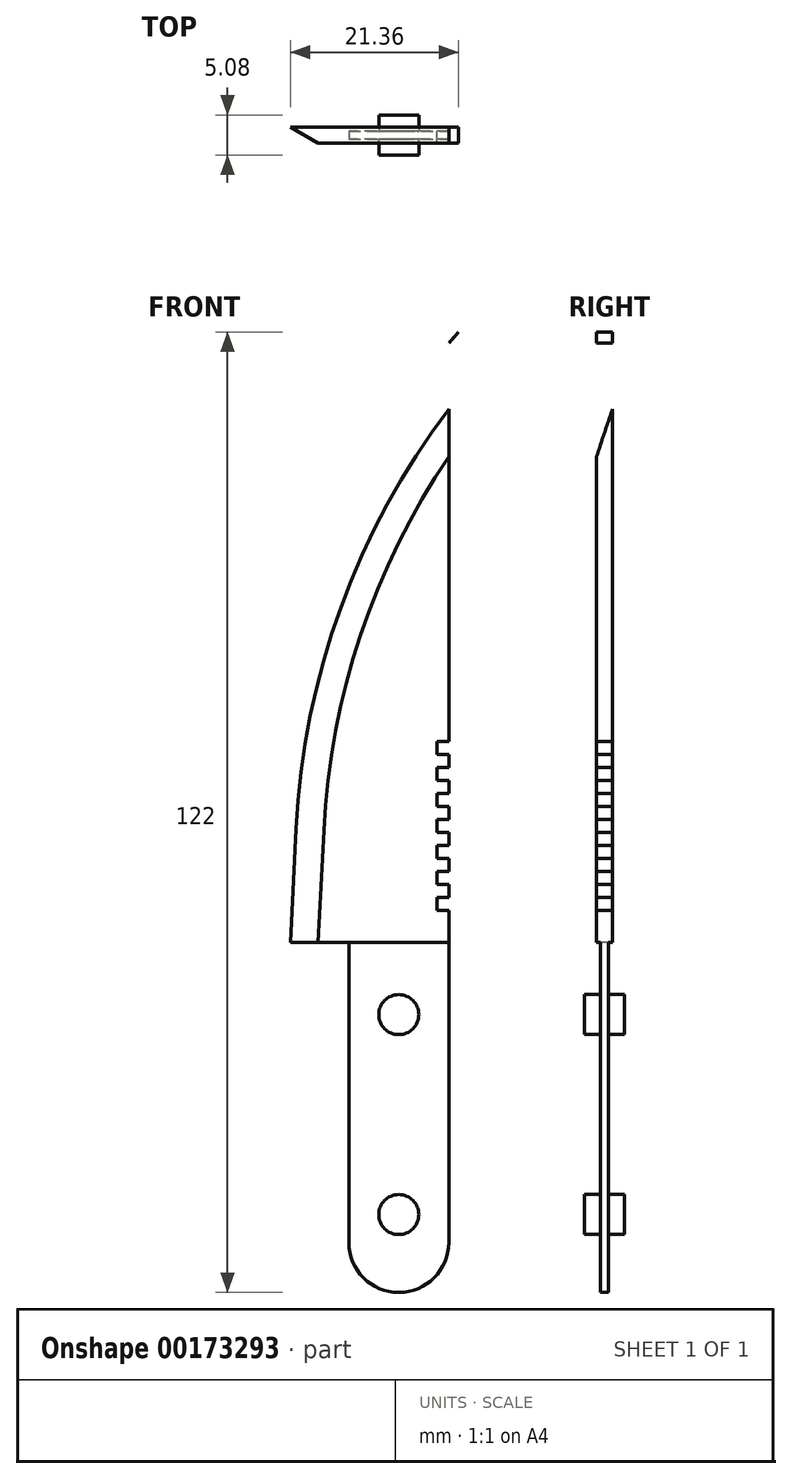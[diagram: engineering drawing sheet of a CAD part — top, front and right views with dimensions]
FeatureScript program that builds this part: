
annotation { "Feature Type Name" : "Feature", "Feature Type Description" : "" }
export const myFeature = defineFeature(function(context is Context, id is Id, definition is map)
    precondition{}
    {
        {
            var Q0;
            Q0=qCreatedBy(makeId("Front.planeOp"),FACE);
            var sketch = newSketch(context, id + "F0", { "sketchPlane" : qUnion([Q0])});
            skLineSegment(sketch, "E0", {"start": v(0, 63.24) * mm, "end": v(1.25, 64.63) * mm});
            skLineSegment(sketch, "E1", {"start": v(0, 63.24) * mm, "end": v(0, 12.64) * mm});
            skLineSegment(sketch, "E2", {"start": v(0, -12.92) * mm, "end": v(-25.4, -12.92) * mm});
            skLineSegment(sketch, "E3", {"start": v(-25.4, -12.92) * mm, "end": v(-24.66, 1.8) * mm});
            skPoint(sketch, "E4.visualSharp", {"position": v(-22.86, 37.81) * mm});
            skArc(sketch, "E4.filletArc", {"start": v(1.25, 64.63) * mm, "mid": v(-17.12, 35.44) * mm, "end": v(-24.66, 1.8) * mm});
            skLineSegment(sketch, "E5.top", {"start": v(-20.95, -18) * mm, "end": v(-4.44, -18) * mm});
            skLineSegment(sketch, "E5.left", {"start": v(-20.95, -12.92) * mm, "end": v(-20.95, -18) * mm});
            skLineSegment(sketch, "E5.right", {"start": v(-4.44, -12.92) * mm, "end": v(-4.44, -18) * mm});
            skLineSegment(sketch, "E6.bottom", {"start": v(0, -8.82) * mm, "end": v(-1.52, -8.82) * mm});
            skLineSegment(sketch, "E6.top", {"start": v(0, -7.17) * mm, "end": v(-1.52, -7.17) * mm});
            skLineSegment(sketch, "E6.right", {"start": v(-1.52, -8.82) * mm, "end": v(-1.52, -7.17) * mm});
            skLineSegment(sketch, "E7.bottom", {"start": v(-1.52, -5.52) * mm, "end": v(0, -5.52) * mm});
            skLineSegment(sketch, "E7.top", {"start": v(-1.52, -3.87) * mm, "end": v(0, -3.87) * mm});
            skLineSegment(sketch, "E7.left", {"start": v(-1.52, -5.52) * mm, "end": v(-1.52, -3.87) * mm});
            skLineSegment(sketch, "E8.bottom", {"start": v(-1.52, -2.21) * mm, "end": v(0, -2.21) * mm});
            skLineSegment(sketch, "E8.top", {"start": v(-1.52, -0.56) * mm, "end": v(0, -0.56) * mm});
            skLineSegment(sketch, "E8.left", {"start": v(-1.52, -2.21) * mm, "end": v(-1.52, -0.56) * mm});
            skLineSegment(sketch, "E9.bottom", {"start": v(-1.52, 1.09) * mm, "end": v(0, 1.09) * mm});
            skLineSegment(sketch, "E9.top", {"start": v(-1.52, 2.74) * mm, "end": v(0, 2.74) * mm});
            skLineSegment(sketch, "E9.left", {"start": v(-1.52, 1.09) * mm, "end": v(-1.52, 2.74) * mm});
            skLineSegment(sketch, "E10", {"start": v(-1.79, 3.56) * mm, "end": v(3.89, 3.56) * mm, "construction": true});
            skLineSegment(sketch, "E11.MirrorCS", {"start": v(-1.52, 4.39) * mm, "end": v(0, 4.39) * mm});
            skLineSegment(sketch, "E12.MirrorCS", {"start": v(-1.52, 6.04) * mm, "end": v(0, 6.04) * mm});
            skLineSegment(sketch, "E13.MirrorCS", {"start": v(-1.52, 6.04) * mm, "end": v(-1.52, 4.39) * mm});
            skLineSegment(sketch, "E14.MirrorCS", {"start": v(-1.52, 7.7) * mm, "end": v(0, 7.7) * mm});
            skLineSegment(sketch, "E15.MirrorCS", {"start": v(-1.52, 9.34) * mm, "end": v(0, 9.34) * mm});
            skLineSegment(sketch, "E16.MirrorCS", {"start": v(-1.52, 9.34) * mm, "end": v(-1.52, 7.7) * mm});
            skLineSegment(sketch, "E17.MirrorCS", {"start": v(-1.52, 11) * mm, "end": v(0, 11) * mm});
            skLineSegment(sketch, "E18.MirrorCS", {"start": v(-1.52, 12.64) * mm, "end": v(0, 12.64) * mm});
            skLineSegment(sketch, "E19.MirrorCS", {"start": v(-1.52, 12.64) * mm, "end": v(-1.52, 11) * mm});
            skPoint(sketch, "E20.orphan", {"position": v(1.5, 12.64) * mm});
            skPoint(sketch, "E21.orphan", {"position": v(1.5, 11) * mm});
            skPoint(sketch, "E22.orphan", {"position": v(1.5, 9.34) * mm});
            skPoint(sketch, "E23.orphan", {"position": v(1.5, 7.7) * mm});
            skPoint(sketch, "E24.orphan", {"position": v(1.5, 6.04) * mm});
            skPoint(sketch, "E25.orphan", {"position": v(1.5, 4.39) * mm});
            skPoint(sketch, "E9.right.end.orphan", {"position": v(1.5, 2.74) * mm});
            skPoint(sketch, "E26.orphan", {"position": v(1.5, 1.09) * mm});
            skPoint(sketch, "E8.right.end.orphan", {"position": v(1.5, -0.56) * mm});
            skPoint(sketch, "E8.right.start.orphan", {"position": v(1.5, -2.21) * mm});
            skPoint(sketch, "E7.right.end.orphan", {"position": v(1.5, -3.87) * mm});
            skPoint(sketch, "E7.right.start.orphan", {"position": v(1.5, -5.52) * mm});
            skLineSegment(sketch, "E27.trimOffspring", {"start": v(0, -5.52) * mm, "end": v(0, -7.17) * mm});
            skLineSegment(sketch, "E28.trimOffspring", {"start": v(0, -8.82) * mm, "end": v(0, -12.92) * mm});
            skLineSegment(sketch, "E29.trimOffspring", {"start": v(0, -2.21) * mm, "end": v(0, -3.87) * mm});
            skLineSegment(sketch, "E30.trimOffspring", {"start": v(0, 1.09) * mm, "end": v(0, -0.56) * mm});
            skLineSegment(sketch, "E31.trimOffspring", {"start": v(0, 4.39) * mm, "end": v(0, 2.74) * mm});
            skLineSegment(sketch, "E32.trimOffspring", {"start": v(0, 7.7) * mm, "end": v(0, 6.04) * mm});
            skLineSegment(sketch, "E33.trimOffspring", {"start": v(0, 11) * mm, "end": v(0, 9.34) * mm});
            skSolve(sketch);
        }
        {
            var Q0;
            Q0=makeQuery(id+"F0.imprint","IMPRINT",FACE,{"disambiguationData":[TD([[makeQuery(id+"F0.imprint","IMPRINT",EDGE,{"derivedFrom":sQuery(id+"F0.wireOp",EDGE,"E0")}),-1.0]])]});
            var Q1;
            {var subQ2=sQuery(id+"F0.wireOp",EDGE,"E3");Q1=makeQuery(id+"F0.imprint","IMPRINT",FACE,{"disambiguationData":[TD([[makeQuery(id+"F0.imprint","IMPRINT",EDGE,{"derivedFrom":subQ2}),-1.0]])]});}
            extrude(context, id + "F1", {"entities" : qUnion([Q0, Q1]), "endBound" : BoundingType.SYMMETRIC, "depth" : 2.03 * mm});
        }
        {
            var Q0;
            Q0=qCreatedBy(makeId("Front.planeOp"),FACE);
            var sketch = newSketch(context, id + "F2", { "sketchPlane" : qUnion([Q0])});
            skLineSegment(sketch, "E34.bottom", {"start": v(-12.7, -11.65) * mm, "end": v(0, -11.65) * mm});
            skLineSegment(sketch, "E34.top", {"start": v(-6.35, -57.37) * mm, "end": v(-6.35, -57.37) * mm});
            skLineSegment(sketch, "E34.left", {"start": v(-12.7, -11.65) * mm, "end": v(-12.7, -51.02) * mm});
            skLineSegment(sketch, "E34.right", {"start": v(0, -11.65) * mm, "end": v(0, -51.02) * mm});
            skPoint(sketch, "E35.visualSharp", {"position": v(-12.7, -57.37) * mm});
            skArc(sketch, "E35.filletArc", {"start": v(-12.7, -51.02) * mm, "mid": v(-10.84, -55.51) * mm, "end": v(-6.35, -57.37) * mm});
            skPoint(sketch, "E36.visualSharp", {"position": v(0, -57.37) * mm});
            skArc(sketch, "E36.filletArc", {"start": v(-6.35, -57.37) * mm, "mid": v(-1.86, -55.51) * mm, "end": v(0, -51.02) * mm});
            skSolve(sketch);
        }
        {
            var Q0;
            Q0=makeQuery(id+"F2.imprint","IMPRINT",FACE,{"disambiguationData":[TD([[makeQuery(id+"F2.imprint","IMPRINT",EDGE,{"derivedFrom":sQuery(id+"F2.wireOp",EDGE,"E34.bottom")}),-1.0]])]});
            extrude(context, id + "F3", {"entities" : qUnion([Q0]), "operationType" : NewBodyOperationType.ADD, "endBound" : BoundingType.SYMMETRIC, "depth" : 1.02 * mm});
        }
        {
            var Q0;
            {var subQ0=sQuery(id+"F2.wireOp",EDGE,"E36.filletArc");var subQ1=sQuery(id+"F2.wireOp",EDGE,"E35.filletArc");var subQ2=sQuery(id+"F2.wireOp",EDGE,"E34.right");var subQ3=sQuery(id+"F2.wireOp",EDGE,"E34.left");var subQ4=makeQuery(id+"F3.opExtrude","CAP_FACE",FACE,{"disambiguationData":[OSD([sQuery(id+"F2.wireOp",EDGE,"E34.bottom"),subQ3,subQ2,subQ1,subQ0])],"isStart":false});Q0=makeQuery(id+"F3.boolean.opBoolean","SPLIT",FACE,{"disambiguationData":[TD([makeQuery(id+"F1.opExtrude","SWEPT_FACE",FACE,{"disambiguationData":[OSD([sQuery(id+"F0.wireOp",EDGE,"E28.trimOffspring")])]})])],"derivedFrom":subQ4});}
            var sketch = newSketch(context, id + "F4", { "sketchPlane" : qUnion([Q0])});
            skCircle(sketch, "E37", {"center": v(-6.35, -22.07) * mm, "radius": 2.54 * mm});
            skCircle(sketch, "E38", {"center": v(-6.35, -47.47) * mm, "radius": 2.54 * mm});
            skSolve(sketch);
        }
        {
            var Q0;
            Q0=makeQuery(id+"F4.imprint","IMPRINT",FACE,{"disambiguationData":[TD([[makeQuery(id+"F4.imprint","IMPRINT",EDGE,{"derivedFrom":sQuery(id+"F4.wireOp",EDGE,"E37")}),1.0]])]});
            var Q1;
            Q1=makeQuery(id+"F4.imprint","IMPRINT",FACE,{"disambiguationData":[TD([[makeQuery(id+"F4.imprint","IMPRINT",EDGE,{"derivedFrom":sQuery(id+"F4.wireOp",EDGE,"E38")}),1.0]])]});
            extrude(context, id + "F5", {"entities" : qUnion([Q0, Q1]), "operationType" : NewBodyOperationType.ADD, "depth" : 2.03 * mm});
        }
        {
            var Q0;
            {var subQ0=sQuery(id+"F2.wireOp",EDGE,"E36.filletArc");var subQ1=sQuery(id+"F2.wireOp",EDGE,"E35.filletArc");var subQ2=sQuery(id+"F2.wireOp",EDGE,"E34.right");var subQ3=sQuery(id+"F2.wireOp",EDGE,"E34.left");var subQ4=makeQuery(id+"F3.opExtrude","CAP_FACE",FACE,{"disambiguationData":[OSD([sQuery(id+"F2.wireOp",EDGE,"E34.bottom"),subQ3,subQ2,subQ1,subQ0])],"isStart":true});Q0=makeQuery(id+"F3.boolean.opBoolean","SPLIT",FACE,{"disambiguationData":[TD([makeQuery(id+"F1.opExtrude","SWEPT_FACE",FACE,{"disambiguationData":[OSD([sQuery(id+"F0.wireOp",EDGE,"E28.trimOffspring")])]})])],"derivedFrom":subQ4});}
            var sketch = newSketch(context, id + "F6", { "sketchPlane" : qUnion([Q0])});
            skCircle(sketch, "E39", {"center": v(6.35, -22.07) * mm, "radius": 2.54 * mm});
            skCircle(sketch, "E40", {"center": v(6.35, -47.47) * mm, "radius": 2.54 * mm});
            skSolve(sketch);
        }
        {
            var Q0;
            Q0=makeQuery(id+"F6.imprint","IMPRINT",FACE,{"disambiguationData":[TD([[makeQuery(id+"F6.imprint","IMPRINT",EDGE,{"derivedFrom":sQuery(id+"F6.wireOp",EDGE,"E40")}),1.0]])]});
            var Q1;
            Q1=makeQuery(id+"F6.imprint","IMPRINT",FACE,{"disambiguationData":[TD([[makeQuery(id+"F6.imprint","IMPRINT",EDGE,{"derivedFrom":sQuery(id+"F6.wireOp",EDGE,"E39")}),1.0]])]});
            extrude(context, id + "F7", {"entities" : qUnion([Q0, Q1]), "operationType" : NewBodyOperationType.ADD, "depth" : 2.03 * mm});
        }
        {
            var Q0;
            Q0=makeQuery(id+"F1.opExtrude","CAP_EDGE",EDGE,{"disambiguationData":[OSD([sQuery(id+"F0.wireOp",EDGE,"E3")])],"isStart":false});
            chamfer(context, id + "F8", {"entities" : qUnion([Q0]), "chamferType" : ChamferType.OFFSET_ANGLE, "width" : 5.08 * mm, "oppositeDirection" : false, "angle" : 60 * degree, "tangentPropagation" : true});
        }
    });
